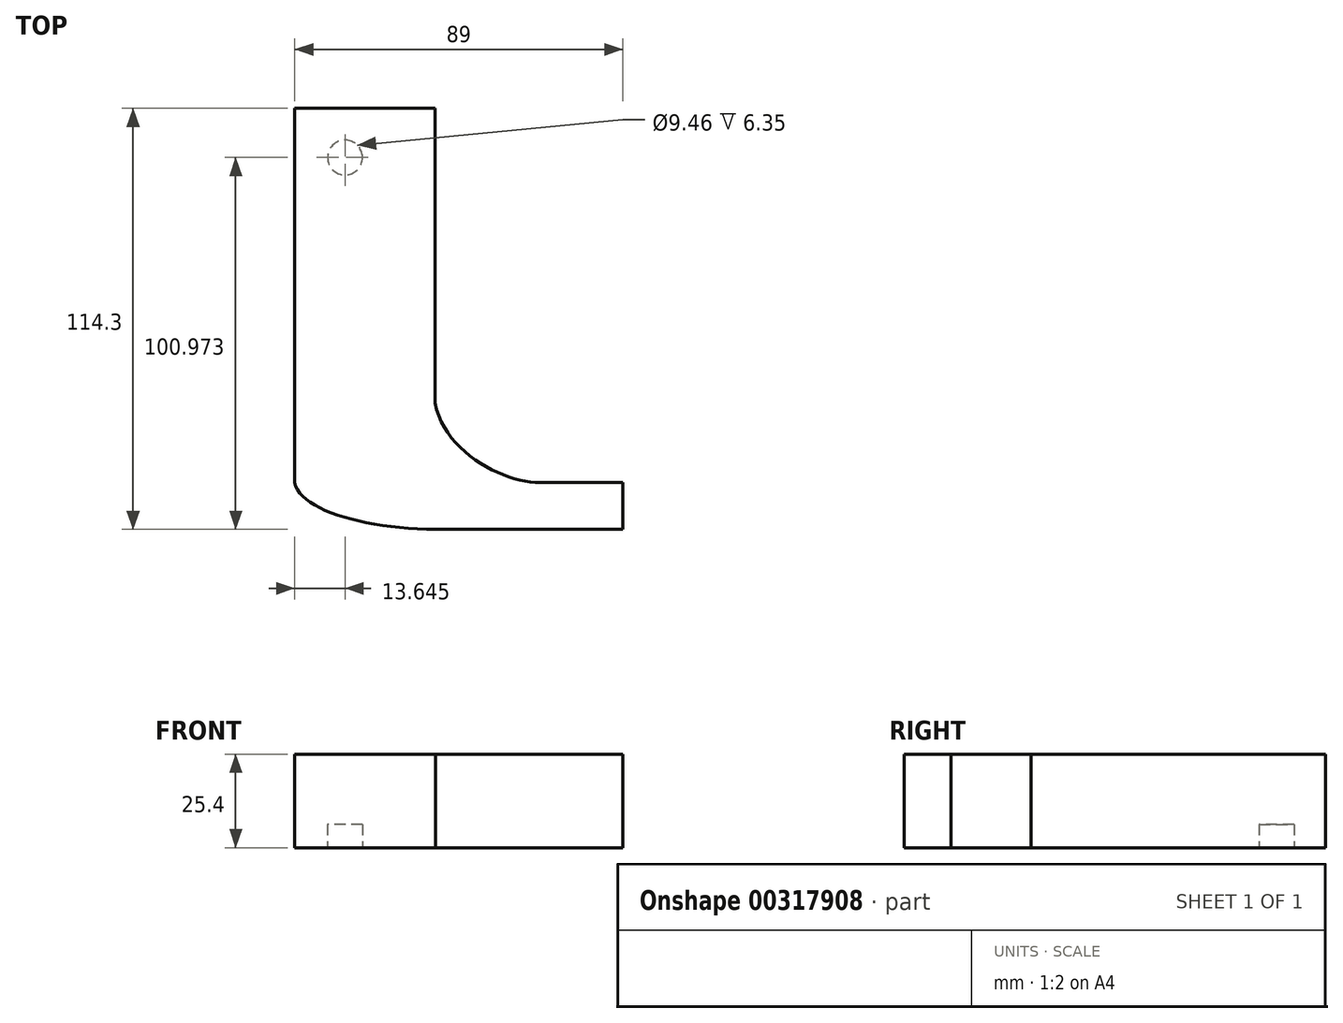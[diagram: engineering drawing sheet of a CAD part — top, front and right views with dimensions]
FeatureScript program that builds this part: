
annotation { "Feature Type Name" : "Feature", "Feature Type Description" : "" }
export const myFeature = defineFeature(function(context is Context, id is Id, definition is map)
    precondition{}
    {
        {
            var Q0;
            Q0=qCreatedBy(makeId("Top.planeOp"),FACE);
            var sketch = newSketch(context, id + "F0", { "sketchPlane" : qUnion([Q0])});
            skLineSegment(sketch, "E0.bottom", {"start": v(-19.05, 50.8) * mm, "end": v(19.05, 50.8) * mm});
            skLineSegment(sketch, "E0.top", {"start": v(-19.05, -50.8) * mm, "end": v(19.05, -50.8) * mm});
            skLineSegment(sketch, "E0.left", {"start": v(-19.05, 50.8) * mm, "end": v(-19.05, -50.8) * mm});
            skLineSegment(sketch, "E0.right", {"start": v(19.05, 50.8) * mm, "end": v(19.05, -50.8) * mm});
            skPoint(sketch, "E0.middle", {"position": v(0, 0) * mm});
            skLineSegment(sketch, "E1.bottom", {"start": v(19.05, -50.8) * mm, "end": v(69.95, -50.8) * mm});
            skLineSegment(sketch, "E1.top", {"start": v(19.16, -63.5) * mm, "end": v(69.95, -63.5) * mm});
            skLineSegment(sketch, "E1.left", {"start": v(19.16, -48.26) * mm, "end": v(19.16, -63.5) * mm});
            skLineSegment(sketch, "E1.right", {"start": v(69.95, -50.8) * mm, "end": v(69.95, -63.5) * mm});
            skPoint(sketch, "E2.1.internal.snap0", {"position": v(19.16, -55.88) * mm});
            skFitSpline(sketch, "E3", {"points": [v(-19.05, -50.8) * mm, v(19.16, -63.5) * mm], "startDerivative": vector(4.52, -22.73) * mm, "endDerivative": vector(57.47, -0.76) * mm});
            skFitSpline(sketch, "E4", {"points": [v(19.05, -29.15) * mm, v(47.49, -50.8) * mm], "startDerivative": vector(7.75, -40.9) * mm, "endDerivative": vector(29.09, 0) * mm});
            skSolve(sketch);
        }
        {
            var Q0;
            Q0 = qSketchRegion(id + "F0", true);
            extrude(context, id + "F1", {"entities" : qUnion([Q0]), "depth" : 25.4 * mm});
        }
        {
            var Q0;
            Q0=qCreatedBy(makeId("Top.planeOp"),FACE);
            var sketch = newSketch(context, id + "F2", { "sketchPlane" : qUnion([Q0])});
            skCircle(sketch, "E5", {"center": v(-5.4, 37.47) * mm, "radius": 4.73 * mm});
            skSolve(sketch);
        }
        {
            var Q0;
            Q0 = qSketchRegion(id + "F2", true);
            extrude(context, id + "F3", {"entities" : qUnion([Q0]), "operationType" : NewBodyOperationType.REMOVE, "endBound" : BoundingType.SYMMETRIC, "depth" : 12.7 * mm});
        }
    });
